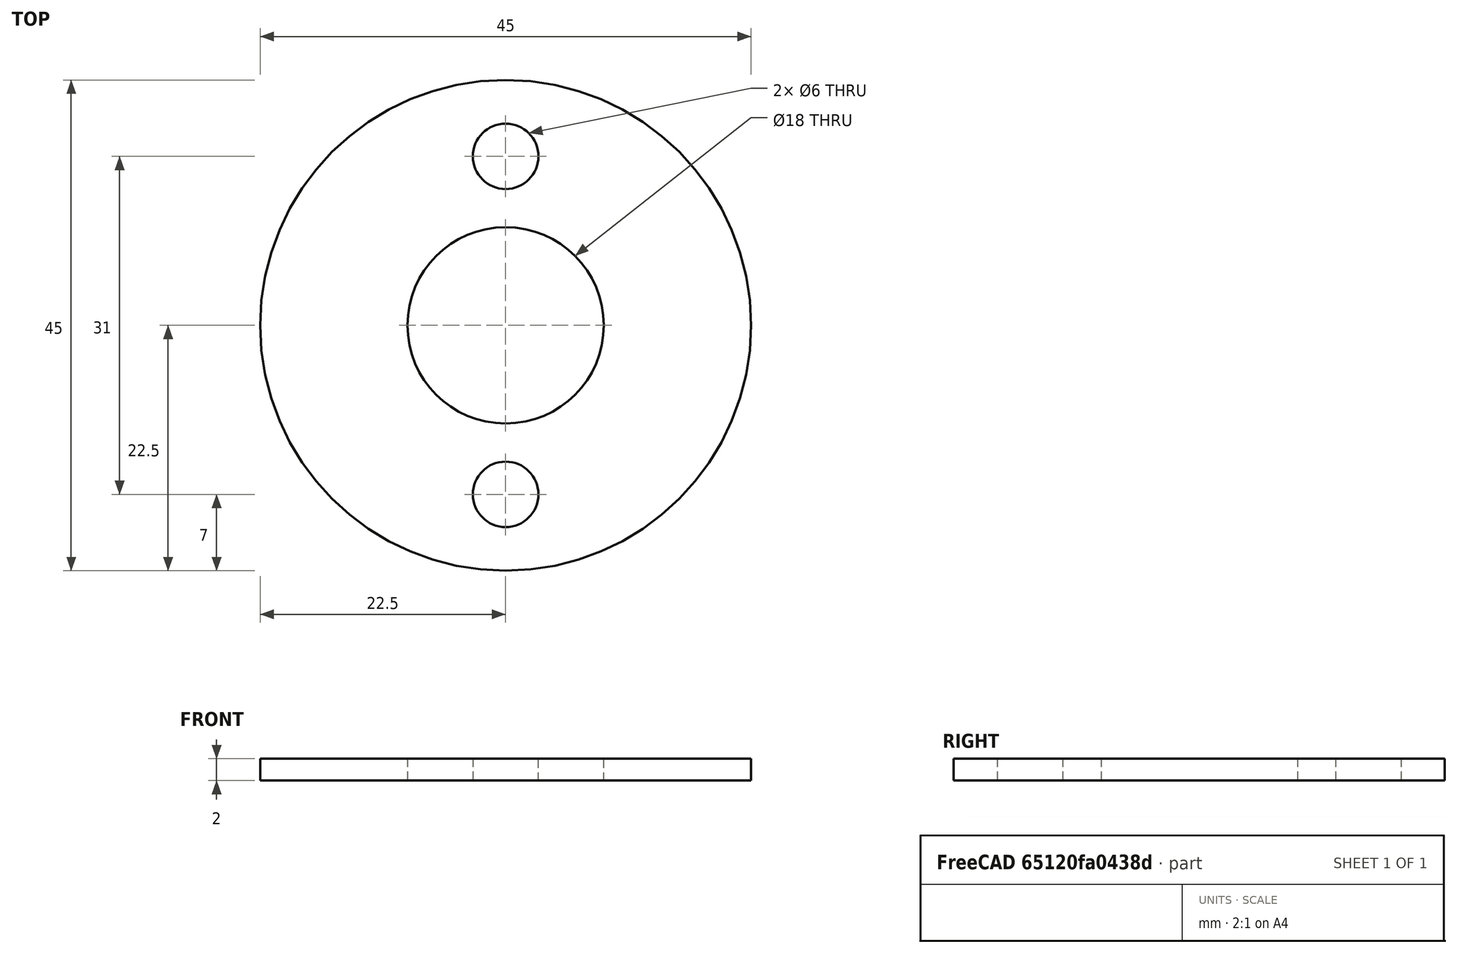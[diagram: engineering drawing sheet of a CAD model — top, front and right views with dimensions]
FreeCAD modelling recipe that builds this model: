
FCSTD DOCUMENT  (FreeCAD 0.16R5861 (Git))
Label: flexywasher
License: All rights reserved
LicenseURL: http://en.wikipedia.org/wiki/All_rights_reserved
objects: Sketcher::SketchObject×1, PartDesign::Pad×1
note: 3 computed .brp shape members not serialized (recipe doc carries the construction recipe); baked Part::Feature solids carry a one-line shape summary decoded from their .brp

FEATURE [Sketcher::SketchObject] Sketch
  sketch-geometry (4):
    g0: Circle CenterX=0 CenterY=0 CenterZ=0 NormalX=0 NormalY=0 NormalZ=1 Radius=22.5
    g1: Circle CenterX=0 CenterY=0 CenterZ=0 NormalX=0 NormalY=0 NormalZ=1 Radius=9
    g2: Circle CenterX=0 CenterY=15.5 CenterZ=0 NormalX=0 NormalY=0 NormalZ=1 Radius=3
    g3: Circle CenterX=0 CenterY=-15.5 CenterZ=0 NormalX=0 NormalY=0 NormalZ=1 Radius=3
  constraints (10):
    c: Coincident(g0,g-1)
    c: Coincident(g1,g-1)
    c: Radius(g0) = 22.5
    c: Radius(g1) = 9
    c: PointOnObject(g2,g-2)
    c: PointOnObject(g3,g-2)
    c: Equal(g2,g3)
    c: DistanceY(g3,g2) = 31
    c: DistanceY(g-1,g3) = -15.5
    c: Radius(g2) = 3
FEATURE [PartDesign::Pad] Pad
  Length = 2
  Length2 = 100
  Sketch = -> Sketch
  Type = 0
